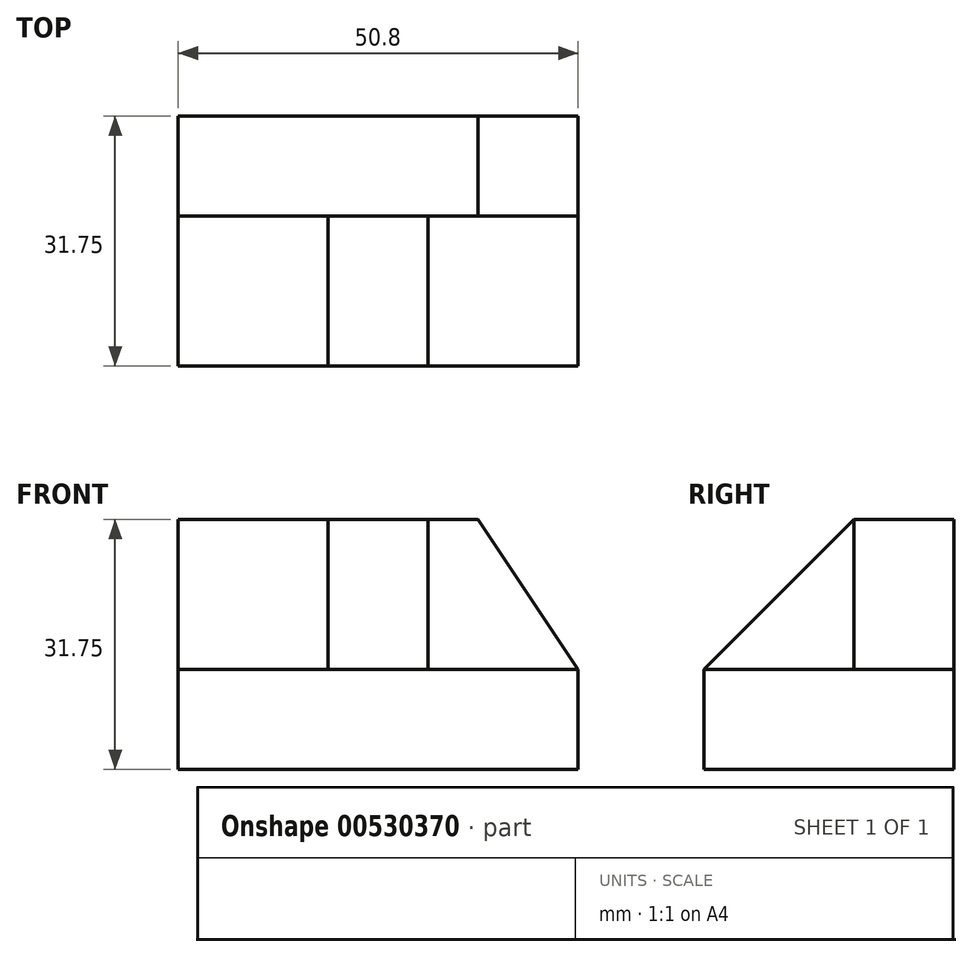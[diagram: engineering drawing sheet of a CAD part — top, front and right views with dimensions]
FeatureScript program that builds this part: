
annotation { "Feature Type Name" : "Feature", "Feature Type Description" : "" }
export const myFeature = defineFeature(function(context is Context, id is Id, definition is map)
    precondition{}
    {
        {
            var Q0;
            Q0=qCreatedBy(makeId("Right.planeOp"),FACE);
            var sketch = newSketch(context, id + "F0", { "sketchPlane" : qUnion([Q0])});
            skLineSegment(sketch, "E0", {"start": v(31.75, 31.75) * mm, "end": v(31.75, 0) * mm});
            skLineSegment(sketch, "E1", {"start": v(31.75, 0) * mm, "end": v(0, 0) * mm});
            skLineSegment(sketch, "E2", {"start": v(0, 0) * mm, "end": v(0, 12.7) * mm});
            skLineSegment(sketch, "E3", {"start": v(0, 12.7) * mm, "end": v(19.05, 12.7) * mm});
            skLineSegment(sketch, "E4", {"start": v(19.05, 12.7) * mm, "end": v(19.05, 31.75) * mm});
            skLineSegment(sketch, "E5", {"start": v(19.05, 31.75) * mm, "end": v(31.75, 31.75) * mm});
            skSolve(sketch);
        }
        {
            var Q0;
            Q0=makeQuery(id+"F0.imprint","IMPRINT",FACE,{"disambiguationData":[TD([[makeQuery(id+"F0.imprint","IMPRINT",EDGE,{"derivedFrom":sQuery(id+"F0.wireOp",EDGE,"E0")}),-1.0]])]});
            extrude(context, id + "F1", {"entities" : qUnion([Q0]), "depth" : 50.8 * mm, "offsetDistance" : 25.4 * mm});
        }
        {
            var Q0;
            Q0=makeQuery(id+"F1.opExtrude","SWEPT_FACE",FACE,{"disambiguationData":[OSD([sQuery(id+"F0.wireOp",EDGE,"E0")])]});
            var sketch = newSketch(context, id + "F2", { "sketchPlane" : qUnion([Q0])});
            skLineSegment(sketch, "E6", {"start": v(-50.8, 31.75) * mm, "end": v(-38.1, 31.75) * mm});
            skLineSegment(sketch, "E7", {"start": v(-38.1, 31.75) * mm, "end": v(-50.8, 12.7) * mm});
            skLineSegment(sketch, "E8", {"start": v(-50.8, 12.7) * mm, "end": v(-50.8, 31.75) * mm});
            skSolve(sketch);
        }
        {
            var Q0;
            Q0=makeQuery(id+"F2.imprint","IMPRINT",FACE,{"disambiguationData":[TD([[makeQuery(id+"F2.imprint","IMPRINT",EDGE,{"derivedFrom":sQuery(id+"F2.wireOp",EDGE,"E6")}),-1.0]])]});
            extrude(context, id + "F3", {"entities" : qUnion([Q0]), "operationType" : NewBodyOperationType.REMOVE, "oppositeDirection" : true, "depth" : 12.7 * mm, "offsetDistance" : 25.4 * mm});
        }
        {
            var Q0;
            Q0=makeQuery(id+"F1.opExtrude","SWEPT_FACE",FACE,{"disambiguationData":[OSD([sQuery(id+"F0.wireOp",EDGE,"E3")])]});
            var sketch = newSketch(context, id + "F4", { "sketchPlane" : qUnion([Q0])});
            skLineSegment(sketch, "E9", {"start": v(31.75, 19.05) * mm, "end": v(31.75, 0) * mm});
            skLineSegment(sketch, "E10", {"start": v(31.75, 0) * mm, "end": v(19.05, 0) * mm});
            skLineSegment(sketch, "E11", {"start": v(19.05, 0) * mm, "end": v(19.05, 19.05) * mm});
            skLineSegment(sketch, "E12", {"start": v(19.05, 19.05) * mm, "end": v(31.75, 19.05) * mm});
            skSolve(sketch);
        }
        {
            var Q0;
            Q0=makeQuery(id+"F4.imprint","IMPRINT",FACE,{"disambiguationData":[TD([[makeQuery(id+"F4.imprint","IMPRINT",EDGE,{"derivedFrom":sQuery(id+"F4.wireOp",EDGE,"E9")}),-1.0]])]});
            extrude(context, id + "F5", {"entities" : qUnion([Q0]), "operationType" : NewBodyOperationType.ADD, "depth" : 19.05 * mm, "offsetDistance" : 25.4 * mm});
        }
        {
            var Q0;
            Q0=makeQuery(id+"F5.opExtrude","SWEPT_FACE",FACE,{"disambiguationData":[OSD([sQuery(id+"F4.wireOp",EDGE,"E9")])]});
            var sketch = newSketch(context, id + "F6", { "sketchPlane" : qUnion([Q0])});
            skLineSegment(sketch, "E13", {"start": v(19.05, 31.75) * mm, "end": v(0, 12.7) * mm});
            skLineSegment(sketch, "E14", {"start": v(0, 12.7) * mm, "end": v(0, 31.75) * mm});
            skLineSegment(sketch, "E15", {"start": v(0, 31.75) * mm, "end": v(19.05, 31.75) * mm});
            skSolve(sketch);
        }
        {
            var Q0;
            Q0=makeQuery(id+"F6.imprint","IMPRINT",FACE,{"disambiguationData":[TD([[makeQuery(id+"F6.imprint","IMPRINT",EDGE,{"derivedFrom":sQuery(id+"F6.wireOp",EDGE,"E13")}),-1.0]])]});
            extrude(context, id + "F7", {"entities" : qUnion([Q0]), "operationType" : NewBodyOperationType.REMOVE, "oppositeDirection" : true, "depth" : 25.4 * mm, "offsetDistance" : 25.4 * mm});
        }
    });
